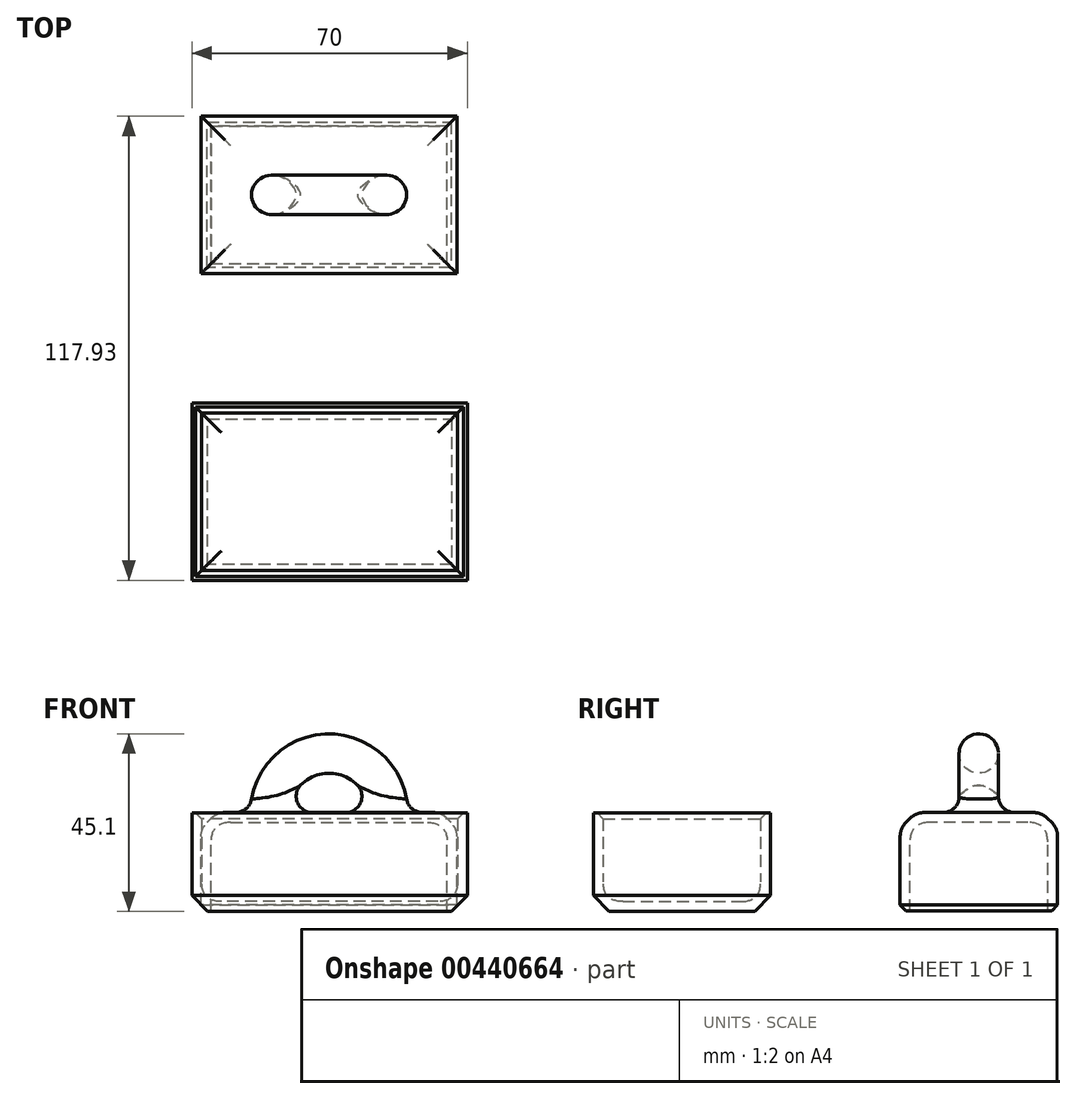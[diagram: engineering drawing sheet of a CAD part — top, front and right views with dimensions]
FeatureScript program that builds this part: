
annotation { "Feature Type Name" : "Feature", "Feature Type Description" : "" }
export const myFeature = defineFeature(function(context is Context, id is Id, definition is map)
    precondition{}
    {
        {
            var Q0;
            Q0=qCreatedBy(makeId("Top.planeOp"),FACE);
            var sketch = newSketch(context, id + "F0", { "sketchPlane" : qUnion([Q0])});
            skLineSegment(sketch, "E0", {"start": v(44.3, -17) * mm, "end": v(44.3, -62) * mm});
            skLineSegment(sketch, "E1", {"start": v(44.3, -62) * mm, "end": v(-25.7, -62) * mm});
            skLineSegment(sketch, "E2", {"start": v(-25.7, -62) * mm, "end": v(-25.7, -17) * mm});
            skLineSegment(sketch, "E3", {"start": v(-25.7, -17) * mm, "end": v(44.3, -17) * mm});
            skSolve(sketch);
        }
        {
            var Q0;
            Q0=makeQuery(id+"F0.imprint","IMPRINT",FACE,{"disambiguationData":[TD([[makeQuery(id+"F0.imprint","IMPRINT",EDGE,{"derivedFrom":sQuery(id+"F0.wireOp",EDGE,"E0")}),-1.0]])]});
            extrude(context, id + "F1", {"entities" : qUnion([Q0]), "depth" : 25 * mm});
        }
        {
            var Q0;
            Q0=makeQuery(id+"F1.opExtrude","CAP_FACE",FACE,{"disambiguationData":[OSD([sQuery(id+"F0.wireOp",EDGE,"E0"),sQuery(id+"F0.wireOp",EDGE,"E1"),sQuery(id+"F0.wireOp",EDGE,"E2"),sQuery(id+"F0.wireOp",EDGE,"E3")])],"isStart":false});
            shell(context, id + "F2", {"entities" : qUnion([Q0]), "thickness" : 2.5 * mm});
        }
        {
            var Q0;
            {var subQ0=sQuery(id+"F0.wireOp",EDGE,"E2");Q0=makeQuery(id+"F2.opShell","OFFSET_EDGE",EDGE,{"disambiguationData":[OSD([subQ0]),TDD([makeQuery(id+"F1.opExtrude","CAP_EDGE",EDGE,{"disambiguationData":[OSD([subQ0])],"isStart":true})])]});}
            var Q1;
            {var subQ0=sQuery(id+"F0.wireOp",EDGE,"E3");Q1=makeQuery(id+"F2.opShell","OFFSET_EDGE",EDGE,{"disambiguationData":[OSD([subQ0]),TDD([makeQuery(id+"F1.opExtrude","CAP_EDGE",EDGE,{"disambiguationData":[OSD([subQ0])],"isStart":true})])]});}
            var Q2;
            {var subQ0=sQuery(id+"F0.wireOp",EDGE,"E0");Q2=makeQuery(id+"F2.opShell","OFFSET_EDGE",EDGE,{"disambiguationData":[OSD([subQ0]),TDD([makeQuery(id+"F1.opExtrude","CAP_EDGE",EDGE,{"disambiguationData":[OSD([subQ0])],"isStart":true})])]});}
            var Q3;
            {var subQ0=sQuery(id+"F0.wireOp",EDGE,"E1");Q3=makeQuery(id+"F2.opShell","OFFSET_EDGE",EDGE,{"disambiguationData":[OSD([subQ0]),TDD([makeQuery(id+"F1.opExtrude","CAP_EDGE",EDGE,{"disambiguationData":[OSD([subQ0])],"isStart":true})])]});}
            fillet(context, id + "F3", {"entities" : qUnion([Q0, Q1, Q2, Q3]), "radius" : 5 * mm, "tangentPropagation" : true, "rho" : 0.5, "crossSection" : FilletCrossSection.CONIC, "allowEdgeOverflow" : false});
        }
        {
            var Q0;
            Q0=makeQuery(id+"F1.opExtrude","CAP_EDGE",EDGE,{"disambiguationData":[OSD([sQuery(id+"F0.wireOp",EDGE,"E1")])],"isStart":true});
            var Q1;
            Q1=makeQuery(id+"F1.opExtrude","CAP_EDGE",EDGE,{"disambiguationData":[OSD([sQuery(id+"F0.wireOp",EDGE,"E2")])],"isStart":true});
            var Q2;
            Q2=makeQuery(id+"F1.opExtrude","CAP_EDGE",EDGE,{"disambiguationData":[OSD([sQuery(id+"F0.wireOp",EDGE,"E0")])],"isStart":true});
            var Q3;
            Q3=makeQuery(id+"F1.opExtrude","CAP_EDGE",EDGE,{"disambiguationData":[OSD([sQuery(id+"F0.wireOp",EDGE,"E3")])],"isStart":true});
            chamfer(context, id + "F4", {"entities" : qUnion([Q0, Q1, Q2, Q3]), "width" : 4 * mm, "tangentPropagation" : true});
        }
        {
            var Q0;
            Q0=qCreatedBy(makeId("Top.planeOp"),FACE);
            var sketch = newSketch(context, id + "F5", { "sketchPlane" : qUnion([Q0])});
            skLineSegment(sketch, "E4.bottom", {"start": v(-23.34, 49.03) * mm, "end": v(41.66, 49.03) * mm});
            skLineSegment(sketch, "E4.top", {"start": v(-23.34, 9.03) * mm, "end": v(41.66, 9.03) * mm});
            skLineSegment(sketch, "E4.left", {"start": v(-23.34, 49.03) * mm, "end": v(-23.34, 9.03) * mm});
            skLineSegment(sketch, "E4.right", {"start": v(41.66, 49.03) * mm, "end": v(41.66, 9.03) * mm});
            skSolve(sketch);
        }
        {
            var Q0;
            Q0=qSketchRegion(id+"F5",true);
            extrude(context, id + "F6", {"entities" : qUnion([Q0]), "depth" : 25 * mm});
        }
        {
            var Q0;
            Q0=makeQuery(id+"F6.opExtrude","CAP_FACE",FACE,{"disambiguationData":[OSD([sQuery(id+"F5.wireOp",EDGE,"E4.bottom"),sQuery(id+"F5.wireOp",EDGE,"E4.top"),sQuery(id+"F5.wireOp",EDGE,"E4.left"),sQuery(id+"F5.wireOp",EDGE,"E4.right")])],"isStart":false});
            shell(context, id + "F7", {"entities" : qUnion([Q0]), "thickness" : 2.5 * mm});
        }
        {
            var Q0;
            {var subQ0=sQuery(id+"F5.wireOp",EDGE,"E4.left");Q0=makeQuery(id+"F7.opShell","OFFSET_EDGE",EDGE,{"disambiguationData":[OSD([subQ0]),TDD([makeQuery(id+"F6.opExtrude","CAP_EDGE",EDGE,{"disambiguationData":[OSD([subQ0])],"isStart":true})])]});}
            var Q1;
            {var subQ0=sQuery(id+"F5.wireOp",EDGE,"E4.top");Q1=makeQuery(id+"F7.opShell","OFFSET_EDGE",EDGE,{"disambiguationData":[OSD([subQ0]),TDD([makeQuery(id+"F6.opExtrude","CAP_EDGE",EDGE,{"disambiguationData":[OSD([subQ0])],"isStart":true})])]});}
            var Q2;
            {var subQ0=sQuery(id+"F5.wireOp",EDGE,"E4.bottom");Q2=makeQuery(id+"F7.opShell","OFFSET_EDGE",EDGE,{"disambiguationData":[OSD([subQ0]),TDD([makeQuery(id+"F6.opExtrude","CAP_EDGE",EDGE,{"disambiguationData":[OSD([subQ0])],"isStart":true})])]});}
            var Q3;
            {var subQ0=sQuery(id+"F5.wireOp",EDGE,"E4.right");Q3=makeQuery(id+"F7.opShell","OFFSET_EDGE",EDGE,{"disambiguationData":[OSD([subQ0]),TDD([makeQuery(id+"F6.opExtrude","CAP_EDGE",EDGE,{"disambiguationData":[OSD([subQ0])],"isStart":true})])]});}
            fillet(context, id + "F8", {"entities" : qUnion([Q0, Q1, Q2, Q3]), "radius" : 5 * mm, "tangentPropagation" : true, "rho" : 0.5, "crossSection" : FilletCrossSection.CONIC, "allowEdgeOverflow" : false});
        }
        {
            var Q0;
            Q0=makeQuery(id+"F6.opExtrude","CAP_EDGE",EDGE,{"disambiguationData":[OSD([sQuery(id+"F5.wireOp",EDGE,"E4.top")])],"isStart":true});
            var Q1;
            Q1=makeQuery(id+"F6.opExtrude","CAP_EDGE",EDGE,{"disambiguationData":[OSD([sQuery(id+"F5.wireOp",EDGE,"E4.left")])],"isStart":true});
            var Q2;
            Q2=makeQuery(id+"F6.opExtrude","CAP_EDGE",EDGE,{"disambiguationData":[OSD([sQuery(id+"F5.wireOp",EDGE,"E4.bottom")])],"isStart":true});
            var Q3;
            Q3=makeQuery(id+"F6.opExtrude","CAP_EDGE",EDGE,{"disambiguationData":[OSD([sQuery(id+"F5.wireOp",EDGE,"E4.right")])],"isStart":true});
            chamfer(context, id + "F9", {"entities" : qUnion([Q0, Q1, Q2, Q3]), "width" : 4 * mm, "tangentPropagation" : true});
        }
        {
            var Q0;
            Q0=makeQuery(id+"F6.opExtrude","SWEPT_BODY",BODY,{"disambiguationData":[OSD([sQuery(id+"F5.wireOp",EDGE,"E4.bottom"),sQuery(id+"F5.wireOp",EDGE,"E4.top"),sQuery(id+"F5.wireOp",EDGE,"E4.left"),sQuery(id+"F5.wireOp",EDGE,"E4.right")])]});
            transform(context, id + "F10", {"entities" : qUnion([Q0]), "transformType" : TransformType.TRANSLATION_3D, "dx" : 0 * mm, "dy" : 0 * mm, "dz" : 26.3 * mm, "makeCopy" : false});
        }
        {
            var Q0;
            Q0=makeQuery(id+"F6.opExtrude","SWEPT_BODY",BODY,{"disambiguationData":[OSD([sQuery(id+"F5.wireOp",EDGE,"E4.bottom"),sQuery(id+"F5.wireOp",EDGE,"E4.top"),sQuery(id+"F5.wireOp",EDGE,"E4.left"),sQuery(id+"F5.wireOp",EDGE,"E4.right")])]});
            var Q1;
            {var subQ0=sQuery(id+"F5.wireOp",EDGE,"E4.bottom");Q1=makeQuery(id+"F9.opChamfer","BLEND_EDGE",EDGE,{"blendedFrom":[makeQuery(id+"F6.opExtrude","CAP_EDGE",EDGE,{"disambiguationData":[OSD([subQ0])],"isStart":true}),makeQuery(id+"F6.opExtrude","CAP_FACE",FACE,{"disambiguationData":[OSD([subQ0,sQuery(id+"F5.wireOp",EDGE,"E4.top"),sQuery(id+"F5.wireOp",EDGE,"E4.left"),sQuery(id+"F5.wireOp",EDGE,"E4.right")])],"isStart":true})],"blendedInto":[makeQuery(id+"F6.opExtrude","CAP_FACE",FACE,{"disambiguationData":[OSD([subQ0,sQuery(id+"F5.wireOp",EDGE,"E4.top"),sQuery(id+"F5.wireOp",EDGE,"E4.left"),sQuery(id+"F5.wireOp",EDGE,"E4.right")])],"isStart":true})]});}
            transform(context, id + "F11", {"entities" : qUnion([Q0]), "transformType" : TransformType.ROTATION, "transformAxis" : qUnion([Q1]), "angle" : 180 * degree, "makeCopy" : false});
        }
        {
            var Q0;
            Q0=makeQuery(id+"F6.opExtrude","SWEPT_BODY",BODY,{"disambiguationData":[OSD([sQuery(id+"F5.wireOp",EDGE,"E4.bottom"),sQuery(id+"F5.wireOp",EDGE,"E4.top"),sQuery(id+"F5.wireOp",EDGE,"E4.left"),sQuery(id+"F5.wireOp",EDGE,"E4.right")])]});
            transform(context, id + "F12", {"entities" : qUnion([Q0]), "transformType" : TransformType.TRANSLATION_3D, "dx" : 0 * mm, "dy" : -25.1 * mm, "dz" : -1.2 * mm, "makeCopy" : false});
        }
        {
            var Q0;
            Q0=makeQuery(id+"F6.opExtrude","CAP_FACE",FACE,{"disambiguationData":[OSD([sQuery(id+"F5.wireOp",EDGE,"E4.bottom"),sQuery(id+"F5.wireOp",EDGE,"E4.top"),sQuery(id+"F5.wireOp",EDGE,"E4.left"),sQuery(id+"F5.wireOp",EDGE,"E4.right")])],"isStart":true});
            var sketch = newSketch(context, id + "F13", { "sketchPlane" : qUnion([Q0])});
            skCircle(sketch, "E5", {"center": v(-5.84, 35.93) * mm, "radius": 5 * mm});
            skCircle(sketch, "E6", {"center": v(24.16, 35.93) * mm, "radius": 5 * mm});
            skLineSegment(sketch, "E7", {"start": v(9.16, 51.93) * mm, "end": v(9.16, 19.93) * mm});
            skPoint(sketch, "E7.endSnap0", {"position": v(9.16, 19.93) * mm});
            skSolve(sketch);
        }
        {
            var Q0;
            Q0 = qSketchRegion(id + "F13", true);
            var Q1;
            Q1=sQuery(id+"F13.wireOp",EDGE,"E7");
            revolve(context, id + "F14", {"operationType" : NewBodyOperationType.ADD, "entities" : qUnion([Q0]), "axis" : qUnion([Q1]), "revolveType" : RevolveType.TWO_DIRECTIONS, "angle" : 120 * degree, "angleBack" : 270 * degree});
        }
        {
            var Q0;
            Q0=makeQuery(id+"F6.opExtrude","CAP_FACE",FACE,{"disambiguationData":[OSD([sQuery(id+"F5.wireOp",EDGE,"E4.bottom"),sQuery(id+"F5.wireOp",EDGE,"E4.top"),sQuery(id+"F5.wireOp",EDGE,"E4.left"),sQuery(id+"F5.wireOp",EDGE,"E4.right")])],"isStart":false});
            var sketch = newSketch(context, id + "F15", { "sketchPlane" : qUnion([Q0])});
            skLineSegment(sketch, "E8.bottom", {"start": v(-11.1, -30.71) * mm, "end": v(29.36, -30.71) * mm});
            skLineSegment(sketch, "E8.top", {"start": v(-11.1, -41.73) * mm, "end": v(29.36, -41.73) * mm});
            skLineSegment(sketch, "E8.left", {"start": v(-11.1, -30.71) * mm, "end": v(-11.1, -41.73) * mm});
            skLineSegment(sketch, "E8.right", {"start": v(29.36, -30.71) * mm, "end": v(29.36, -41.73) * mm});
            skSolve(sketch);
        }
        {
            var Q0;
            Q0=makeQuery(id+"F15.imprint","IMPRINT",FACE,{"disambiguationData":[TD([[makeQuery(id+"F15.imprint","IMPRINT",EDGE,{"derivedFrom":sQuery(id+"F15.wireOp",EDGE,"E8.bottom")}),-1.0]])]});
            extrude(context, id + "F16", {"entities" : qUnion([Q0]), "operationType" : NewBodyOperationType.REMOVE, "oppositeDirection" : true, "depth" : 22.5 * mm});
        }
        {
            var Q0;
            {var subQ0=sQuery(id+"F5.wireOp",EDGE,"E4.bottom");Q0=makeQuery(id+"F9.opChamfer","BLEND_EDGE",EDGE,{"blendedFrom":[makeQuery(id+"F6.opExtrude","CAP_EDGE",EDGE,{"disambiguationData":[OSD([subQ0])],"isStart":true}),makeQuery(id+"F6.opExtrude","CAP_FACE",FACE,{"disambiguationData":[OSD([subQ0,sQuery(id+"F5.wireOp",EDGE,"E4.top"),sQuery(id+"F5.wireOp",EDGE,"E4.left"),sQuery(id+"F5.wireOp",EDGE,"E4.right")])],"isStart":true})],"blendedInto":[makeQuery(id+"F6.opExtrude","CAP_FACE",FACE,{"disambiguationData":[OSD([subQ0,sQuery(id+"F5.wireOp",EDGE,"E4.top"),sQuery(id+"F5.wireOp",EDGE,"E4.left"),sQuery(id+"F5.wireOp",EDGE,"E4.right")])],"isStart":true})]});}
            var Q1;
            {var subQ0=sQuery(id+"F5.wireOp",EDGE,"E4.right");Q1=makeQuery(id+"F9.opChamfer","BLEND_EDGE",EDGE,{"blendedFrom":[makeQuery(id+"F6.opExtrude","CAP_EDGE",EDGE,{"disambiguationData":[OSD([subQ0])],"isStart":true}),makeQuery(id+"F6.opExtrude","CAP_FACE",FACE,{"disambiguationData":[OSD([sQuery(id+"F5.wireOp",EDGE,"E4.bottom"),sQuery(id+"F5.wireOp",EDGE,"E4.top"),sQuery(id+"F5.wireOp",EDGE,"E4.left"),subQ0])],"isStart":true})],"blendedInto":[makeQuery(id+"F6.opExtrude","CAP_FACE",FACE,{"disambiguationData":[OSD([sQuery(id+"F5.wireOp",EDGE,"E4.bottom"),sQuery(id+"F5.wireOp",EDGE,"E4.top"),sQuery(id+"F5.wireOp",EDGE,"E4.left"),subQ0])],"isStart":true})]});}
            var Q2;
            {var subQ0=sQuery(id+"F5.wireOp",EDGE,"E4.top");Q2=makeQuery(id+"F9.opChamfer","BLEND_EDGE",EDGE,{"blendedFrom":[makeQuery(id+"F6.opExtrude","CAP_EDGE",EDGE,{"disambiguationData":[OSD([subQ0])],"isStart":true}),makeQuery(id+"F6.opExtrude","CAP_FACE",FACE,{"disambiguationData":[OSD([sQuery(id+"F5.wireOp",EDGE,"E4.bottom"),subQ0,sQuery(id+"F5.wireOp",EDGE,"E4.left"),sQuery(id+"F5.wireOp",EDGE,"E4.right")])],"isStart":true})],"blendedInto":[makeQuery(id+"F6.opExtrude","CAP_FACE",FACE,{"disambiguationData":[OSD([sQuery(id+"F5.wireOp",EDGE,"E4.bottom"),subQ0,sQuery(id+"F5.wireOp",EDGE,"E4.left"),sQuery(id+"F5.wireOp",EDGE,"E4.right")])],"isStart":true})]});}
            var Q3;
            {var subQ0=sQuery(id+"F5.wireOp",EDGE,"E4.left");Q3=makeQuery(id+"F9.opChamfer","BLEND_EDGE",EDGE,{"blendedFrom":[makeQuery(id+"F6.opExtrude","CAP_EDGE",EDGE,{"disambiguationData":[OSD([subQ0])],"isStart":true}),makeQuery(id+"F6.opExtrude","CAP_FACE",FACE,{"disambiguationData":[OSD([sQuery(id+"F5.wireOp",EDGE,"E4.bottom"),sQuery(id+"F5.wireOp",EDGE,"E4.top"),subQ0,sQuery(id+"F5.wireOp",EDGE,"E4.right")])],"isStart":true})],"blendedInto":[makeQuery(id+"F6.opExtrude","CAP_FACE",FACE,{"disambiguationData":[OSD([sQuery(id+"F5.wireOp",EDGE,"E4.bottom"),sQuery(id+"F5.wireOp",EDGE,"E4.top"),subQ0,sQuery(id+"F5.wireOp",EDGE,"E4.right")])],"isStart":true})]});}
            var Q4;
            {var subQ0=sQuery(id+"F5.wireOp",EDGE,"E4.right");Q4=makeQuery(id+"F9.opChamfer","BLEND_EDGE",EDGE,{"blendedFrom":[makeQuery(id+"F6.opExtrude","CAP_EDGE",EDGE,{"disambiguationData":[OSD([subQ0])],"isStart":true}),makeQuery(id+"F6.opExtrude","SWEPT_FACE",FACE,{"disambiguationData":[OSD([subQ0])]})],"blendedInto":[makeQuery(id+"F6.opExtrude","SWEPT_FACE",FACE,{"disambiguationData":[OSD([subQ0])]})]});}
            var Q5;
            {var subQ0=sQuery(id+"F5.wireOp",EDGE,"E4.top");Q5=makeQuery(id+"F9.opChamfer","BLEND_EDGE",EDGE,{"blendedFrom":[makeQuery(id+"F6.opExtrude","CAP_EDGE",EDGE,{"disambiguationData":[OSD([subQ0])],"isStart":true}),makeQuery(id+"F6.opExtrude","SWEPT_FACE",FACE,{"disambiguationData":[OSD([subQ0])]})],"blendedInto":[makeQuery(id+"F6.opExtrude","SWEPT_FACE",FACE,{"disambiguationData":[OSD([subQ0])]})]});}
            var Q6;
            {var subQ0=sQuery(id+"F5.wireOp",EDGE,"E4.left");Q6=makeQuery(id+"F9.opChamfer","BLEND_EDGE",EDGE,{"blendedFrom":[makeQuery(id+"F6.opExtrude","CAP_EDGE",EDGE,{"disambiguationData":[OSD([subQ0])],"isStart":true}),makeQuery(id+"F6.opExtrude","SWEPT_FACE",FACE,{"disambiguationData":[OSD([subQ0])]})],"blendedInto":[makeQuery(id+"F6.opExtrude","SWEPT_FACE",FACE,{"disambiguationData":[OSD([subQ0])]})]});}
            var Q7;
            {var subQ0=sQuery(id+"F5.wireOp",EDGE,"E4.bottom");Q7=makeQuery(id+"F9.opChamfer","BLEND_EDGE",EDGE,{"blendedFrom":[makeQuery(id+"F6.opExtrude","CAP_EDGE",EDGE,{"disambiguationData":[OSD([subQ0])],"isStart":true}),makeQuery(id+"F6.opExtrude","SWEPT_FACE",FACE,{"disambiguationData":[OSD([subQ0])]})],"blendedInto":[makeQuery(id+"F6.opExtrude","SWEPT_FACE",FACE,{"disambiguationData":[OSD([subQ0])]})]});}
            fillet(context, id + "F17", {"entities" : qUnion([Q0, Q1, Q2, Q3, Q4, Q5, Q6, Q7]), "radius" : 5 * mm, "tangentPropagation" : true, "allowEdgeOverflow" : false});
        }
        {
            var Q0;
            Q0=makeQuery(id+"F14.boolean.opBoolean","MERGE",FACE,{"disambiguationData":[OD(1.0)],"derivedFrom":[makeQuery(id+"F14.opRevolve","SWEPT_FACE",FACE,{"disambiguationData":[OSD([sQuery(id+"F13.wireOp",EDGE,"E5")])]}),makeQuery(id+"F14.opRevolve","SWEPT_FACE",FACE,{"disambiguationData":[OSD([sQuery(id+"F13.wireOp",EDGE,"E6")])]})]});
            fillet(context, id + "F18", {"entities" : qUnion([Q0]), "radius" : 4.1 * mm, "tangentPropagation" : true, "allowEdgeOverflow" : false});
        }
        {
            var Q0;
            {var subQ0=sQuery(id+"F0.wireOp",EDGE,"E3");Q0=makeQuery(id+"F2.opShell","OFFSET_EDGE",EDGE,{"disambiguationData":[OSD([subQ0]),TDD([makeQuery(id+"F1.opExtrude","CAP_EDGE",EDGE,{"disambiguationData":[OSD([subQ0])],"isStart":false})])]});}
            var Q1;
            {var subQ0=sQuery(id+"F0.wireOp",EDGE,"E2");Q1=makeQuery(id+"F2.opShell","OFFSET_EDGE",EDGE,{"disambiguationData":[OSD([subQ0]),TDD([makeQuery(id+"F1.opExtrude","CAP_EDGE",EDGE,{"disambiguationData":[OSD([subQ0])],"isStart":false})])]});}
            var Q2;
            {var subQ0=sQuery(id+"F0.wireOp",EDGE,"E1");Q2=makeQuery(id+"F2.opShell","OFFSET_EDGE",EDGE,{"disambiguationData":[OSD([subQ0]),TDD([makeQuery(id+"F1.opExtrude","CAP_EDGE",EDGE,{"disambiguationData":[OSD([subQ0])],"isStart":false})])]});}
            var Q3;
            {var subQ0=sQuery(id+"F0.wireOp",EDGE,"E0");Q3=makeQuery(id+"F2.opShell","OFFSET_EDGE",EDGE,{"disambiguationData":[OSD([subQ0]),TDD([makeQuery(id+"F1.opExtrude","CAP_EDGE",EDGE,{"disambiguationData":[OSD([subQ0])],"isStart":false})])]});}
            chamfer(context, id + "F19", {"entities" : qUnion([Q0, Q1, Q2, Q3]), "width" : 1.5 * mm, "tangentPropagation" : true});
        }
        {
            var Q0;
            Q0=makeQuery(id+"F6.opExtrude","CAP_EDGE",EDGE,{"disambiguationData":[OSD([sQuery(id+"F5.wireOp",EDGE,"E4.top")])],"isStart":false});
            var Q1;
            Q1=makeQuery(id+"F6.opExtrude","CAP_EDGE",EDGE,{"disambiguationData":[OSD([sQuery(id+"F5.wireOp",EDGE,"E4.left")])],"isStart":false});
            var Q2;
            Q2=makeQuery(id+"F6.opExtrude","CAP_EDGE",EDGE,{"disambiguationData":[OSD([sQuery(id+"F5.wireOp",EDGE,"E4.right")])],"isStart":false});
            var Q3;
            Q3=makeQuery(id+"F6.opExtrude","CAP_EDGE",EDGE,{"disambiguationData":[OSD([sQuery(id+"F5.wireOp",EDGE,"E4.bottom")])],"isStart":false});
            chamfer(context, id + "F20", {"entities" : qUnion([Q0, Q1, Q2, Q3]), "width" : 1.5 * mm, "tangentPropagation" : true});
        }
    });
